# Revit family: QF_ELECTROLUXPROFESSIONAL_520529_EHT60XLG-ESD
name_source: partatom
category: Specialty Equipment
units: mm (PartAtom-declared; Revit-internal decimal feet)

## family parameters
Always vertical = Yes
Cut with Voids When Loaded = No
Part Type = Normal
Room Calculation Point = No
Round Connector Dimension = Use Diameter
Shared = Yes
Work Plane-Based = No

## types (1)
- Standard
    Accessory = Yes
    Default Elevation = 0 mm  [stored 0 ft]
    Depth Actual = 988 mm
    Description = HOOD TYPE XL DISHWASHER, 60R/H,KFC
    Height Actual = 1567 mm  [stored 5.14108 ft]
    Item Number = 520529
    Length Actual = 990 mm  [stored 3.24803 ft]
    Manufacturer = Electrolux Professional
    Model = EHT60XLG-ESD
    URL = http://professional.electrolux.com
    URL Manufacturer = http://professional.electrolux.com
    Weight = 135.00 kg

note: [stored X ft] marks values corroborated as IEEE doubles in the binary element streams (Revit-internal decimal feet)

## geometry (parser evidence)
native form markers: Sweep x2
no freeform markers — native parametric forms only
